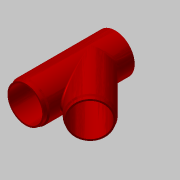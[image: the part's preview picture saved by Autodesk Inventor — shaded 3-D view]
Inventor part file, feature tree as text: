
AUTODESK INVENTOR PART (.ipt)
format: ipt  version: 2017.3 (Build 213257000, 257)  size: 334,336 bytes
history: native  units: in
note: dims shown in document units (in); Inventor stores cm internally (conversion verified against a paired STEP export)
features: extrude x18, sketch x15, fillet x6, chamfer x3, projected_geometry x2, plane x1, revolve x1
ambient origin geometry x8: Origin, YZ Plane, XZ Plane, XY Plane, X Axis, Y Axis, Z Axis, Center Point
bodies: Solid1 (feature_tree)
feature tree (46):
  sketch  "Sketch1"  dims[d0=26.5in d1=29.0in]
  extrude  "Extrusion1"  Depth=29.0in
  plane  "Work Plane1"
  sketch  "Sketch2"  dims[d2=31.0in d3=50.9921in d4=19.4961in d5=0.0in d6=0.0in]
  extrude  "Extrusion2"  Depth=50.9921in TaperAngle=0.0deg
  extrude  "Extrusion3"  Depth=26.5in
  extrude  "Extrusion4"  Depth=31.0in
  extrude  "Extrusion5"  Depth=28.0in
  extrude  "Extrusion6"  Depth=28.0in
  extrude  "Extrusion7"  TaperAngle=0.0deg  [1 undecoded]
  extrude  "Extrusion8"  Depth=0.5in
  extrude  "Extrusion9"  Depth=47.9921in
  fillet  "Fillet1"  Radius=16.4961in
  fillet  "Fillet2"  [1 undecoded]
  fillet  "Fillet3"  Radius=47.9921in
  fillet  "Fillet4"  [1 undecoded]
  extrude  "Extrusion10"  TaperAngle=0.0deg  [1 undecoded]
  extrude  "Extrusion11"  TaperAngle=0.0deg  [1 undecoded]
  extrude  "Extrusion12"  Depth=6.0in
  fillet  "Fillet5"  Radius=1.0in
  chamfer  "Chamfer3"  Distance=1.0in
  fillet  "Fillet6"  Radius=30.48in
  chamfer  "Chamfer4"  Distance=1.0in
  extrude  "Extrusion15"  Depth=1.0in TaperAngle=0.0deg
  extrude  "Extrusion17"  Depth=0.0312in
  extrude  "Extrusion19"  Depth=0.74in
  chamfer  "Chamfer6"  Distance=0.125in Angle=45.0deg
  extrude  "Extrusion21"  Depth=0.0312in
  extrude  "Extrusion22"  Depth=0.0312in TaperAngle=45.0deg
  extrude  "Extrusion23"  Depth=1.0in TaperAngle=0.0deg
  revolve  "Revolution1"  [1 undecoded]
  sketch  "Sketch3"  dims[d7=45.0deg d8=26.5in]
  sketch  "Sketch4"  dims[d9=29.0in d10=31.0in]
  sketch  "Sketch5"  dims[d11=50.9921in d12=0.0in d13=28.0in]
  sketch  "Sketch6"  dims[d14=0.5in d15=0.0in d16=28.0in]
  sketch  "Sketch7"  dims[d17=0.5in d18=0.0in]
  sketch  "Sketch8"  dims[d19=28.0in d20=0.5in]
  sketch  "Sketch11"  dims[d21=0.0in d22=47.9921in d23=16.4961in d24=0.0in d25=0.0in d26=47.9921in d27=0.0in]
  sketch  "Sketch13"  dims[d28=50.9921in d29=0.0in]
  projected_geometry  "Projected Loop4"
  sketch  "Sketch15"  dims[d30=50.9921in d31=0.0in]
  sketch  "Sketch17"  dims[d32=1.0in d33=6.0in d34=1.0in]
  sketch  "Sketch18"  dims[d35=1.0in]
  sketch  "Sketch19"  dims[d39=30.48in d40=1.0in d41=0.0in d42=30.48in d43=1.0in d44=0.0in]
  sketch  "Sketch21"  dims[d45=30.48in d46=1.0in d47=0.0in d48=0.0312in d52=0.74in d53=0.125in d54=45.0deg d55=0.0312in d56=0.0312in d57=0.125in d58=45.0deg d66=1.0in d67=0.0in d76=1.0in d77=0.0in d83=1.0in d84=0.0in d85=0.26in d86=0.125in d87=45.0deg d93=1.0in d94=0.0in d95=1.0in d96=0.0in d97=1.0in d98=0.0in d99=90.0deg]
  projected_geometry  "Project Cut Edges1"
note: 6 required parameter values undecoded (feature->parameter linkage not recoverable at this tier; creation-order binding heuristic only, values carry confidence <= 0.55)